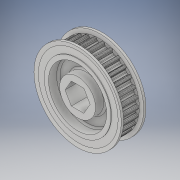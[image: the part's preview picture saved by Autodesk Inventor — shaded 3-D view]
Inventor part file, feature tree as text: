
AUTODESK INVENTOR PART (.ipt)
format: ipt  version: 2018 (Build 220112000, 112)  size: 940,032 bytes
history: native  units: in
note: dims shown in document units (in); Inventor stores cm internally (conversion verified against a paired STEP export)
features: mirror x1
ambient origin geometry x8: Origin, YZ Plane, XZ Plane, XY Plane, X Axis, Y Axis, Z Axis, Center Point
bodies: Solid1 (feature_tree)
feature tree (1):
  mirror  "Mirror1"
